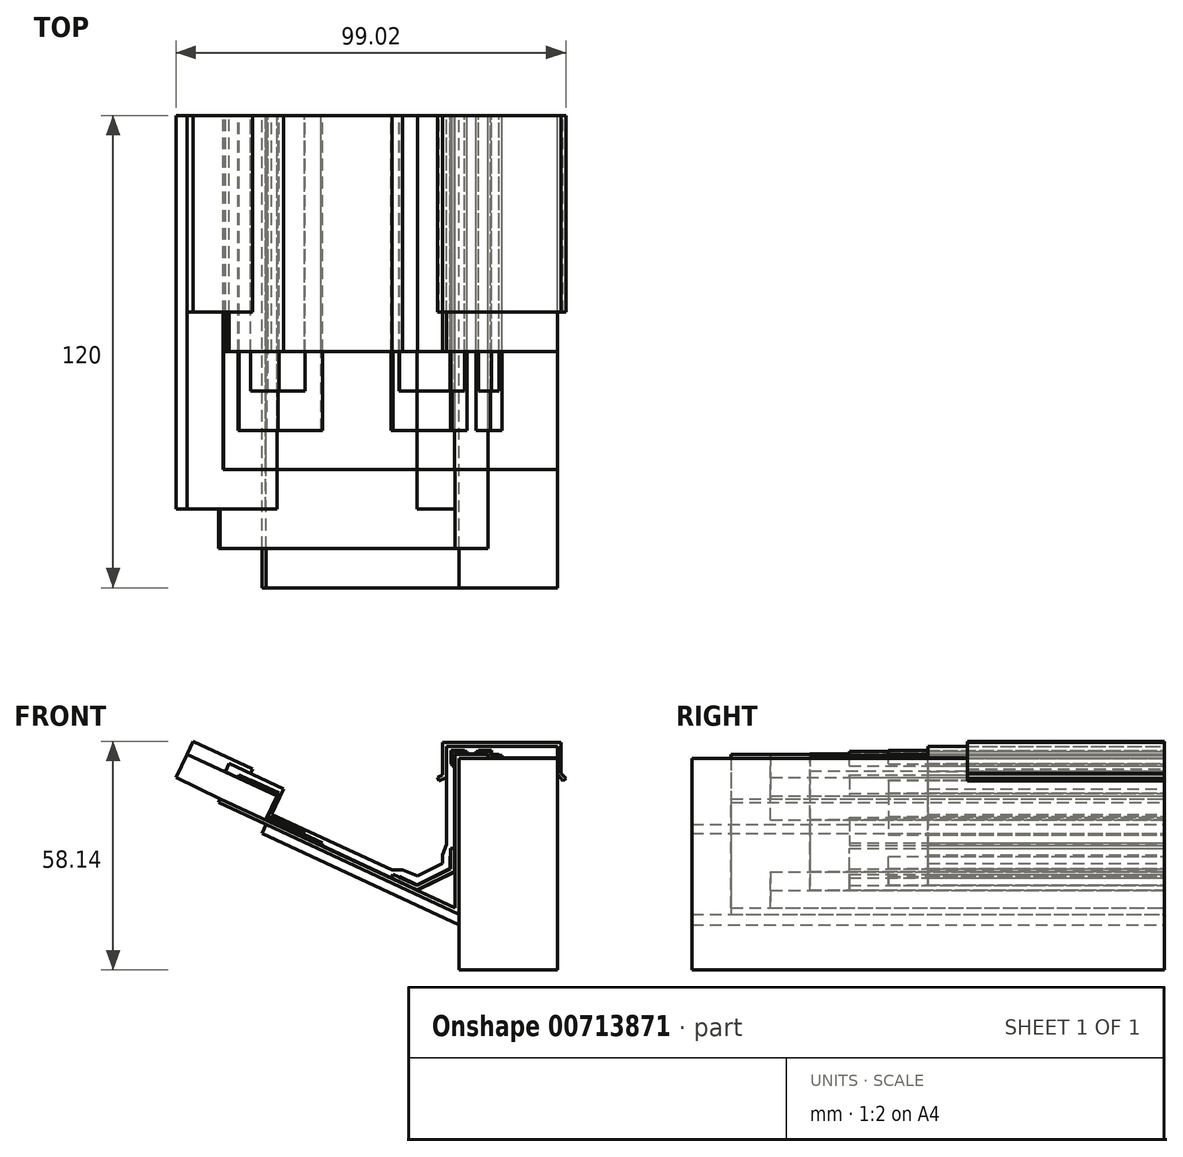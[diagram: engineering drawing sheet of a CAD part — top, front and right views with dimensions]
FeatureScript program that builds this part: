
annotation { "Feature Type Name" : "Feature", "Feature Type Description" : "" }
export const myFeature = defineFeature(function(context is Context, id is Id, definition is map)
    precondition{}
    {
        {
            var Q0;
            Q0=qCreatedBy(makeId("Front.planeOp"),FACE);
            var sketch = newSketch(context, id + "F0", { "sketchPlane" : qUnion([Q0])});
            skLineSegment(sketch, "E0.bottom", {"start": v(37.75, 38) * mm, "end": v(62.75, 38) * mm});
            skLineSegment(sketch, "E0.top", {"start": v(37.75, -15.78) * mm, "end": v(62.75, -15.78) * mm});
            skLineSegment(sketch, "E0.left", {"start": v(37.75, 38) * mm, "end": v(37.75, -15.78) * mm});
            skLineSegment(sketch, "E0.right", {"start": v(62.75, 38) * mm, "end": v(62.75, -15.78) * mm});
            skLineSegment(sketch, "E1", {"start": v(45.13, 38) * mm, "end": v(45.13, 39) * mm});
            skLineSegment(sketch, "E2", {"start": v(45.13, 39) * mm, "end": v(36.75, 39) * mm});
            skLineSegment(sketch, "E3", {"start": v(36.75, 39) * mm, "end": v(36.75, 0) * mm});
            skLineSegment(sketch, "E4", {"start": v(36.75, 0) * mm, "end": v(-22.92, 27.76) * mm});
            skLineSegment(sketch, "E5", {"start": v(-22.92, 27.76) * mm, "end": v(-23.34, 26.86) * mm});
            skLineSegment(sketch, "E6", {"start": v(-23.34, 26.86) * mm, "end": v(37.75, -1.57) * mm});
            skLineSegment(sketch, "E7", {"start": v(37.75, 38) * mm, "end": v(37.75, 40.22) * mm, "construction": true});
            skLineSegment(sketch, "E8", {"start": v(-11.3, 22.36) * mm, "end": v(-8.48, 28.43) * mm});
            skLineSegment(sketch, "E9", {"start": v(-8.48, 28.43) * mm, "end": v(-31.34, 39.07) * mm});
            skLineSegment(sketch, "E10", {"start": v(-31.34, 39.07) * mm, "end": v(-34.1, 33.15) * mm});
            skLineSegment(sketch, "E11", {"start": v(-34.1, 33.15) * mm, "end": v(-22.92, 27.76) * mm});
            skLineSegment(sketch, "E12", {"start": v(-11.24, 21.23) * mm, "end": v(-12.29, 18.98) * mm});
            skLineSegment(sketch, "E13", {"start": v(-12.29, 18.98) * mm, "end": v(37.75, -4.3) * mm});
            skLineSegment(sketch, "E14", {"start": v(27.16, 4.46) * mm, "end": v(36.75, 9.19) * mm});
            skLineSegment(sketch, "E15", {"start": v(-22.13, 34.79) * mm, "end": v(-22.09, 34.88) * mm});
            skLineSegment(sketch, "E16", {"start": v(-22.09, 34.88) * mm, "end": v(-8.43, 28.52) * mm});
            skLineSegment(sketch, "E17", {"start": v(-8.43, 28.52) * mm, "end": v(-8.48, 28.43) * mm});
            skLineSegment(sketch, "E18", {"start": v(-11.26, 22.45) * mm, "end": v(27.16, 4.57) * mm});
            skLineSegment(sketch, "E19", {"start": v(27.16, 4.57) * mm, "end": v(36.65, 9.25) * mm});
            skLineSegment(sketch, "E20", {"start": v(36.65, 9.25) * mm, "end": v(36.65, 39.1) * mm});
            skLineSegment(sketch, "E21", {"start": v(36.65, 39.1) * mm, "end": v(45.13, 39.1) * mm});
            skLineSegment(sketch, "E22", {"start": v(45.13, 39.1) * mm, "end": v(45.13, 39) * mm});
            skLineSegment(sketch, "E23", {"start": v(36.75, 39) * mm, "end": v(36.75, 39.77) * mm, "construction": true});
            skLineSegment(sketch, "E24", {"start": v(27.16, 4.57) * mm, "end": v(27.2, 4.48) * mm, "construction": true});
            skLineSegment(sketch, "E25", {"start": v(-18.36, 33.14) * mm, "end": v(-18.08, 33.75) * mm});
            skLineSegment(sketch, "E26", {"start": v(-18.08, 33.75) * mm, "end": v(-8.15, 29.13) * mm});
            skLineSegment(sketch, "E27", {"start": v(-8.15, 29.13) * mm, "end": v(-8.43, 28.52) * mm});
            skLineSegment(sketch, "E28", {"start": v(-10.98, 23.06) * mm, "end": v(3.07, 16.52) * mm});
            skLineSegment(sketch, "E29", {"start": v(3.07, 16.52) * mm, "end": v(2.79, 15.91) * mm});
            skLineSegment(sketch, "E30", {"start": v(-15.18, 32.4) * mm, "end": v(-15.1, 32.58) * mm});
            skLineSegment(sketch, "E31", {"start": v(-15.1, 32.58) * mm, "end": v(-7.89, 29.23) * mm});
            skLineSegment(sketch, "E32", {"start": v(-7.89, 29.23) * mm, "end": v(-10.67, 23.25) * mm});
            skLineSegment(sketch, "E33", {"start": v(-10.67, 23.25) * mm, "end": v(-1.32, 18.9) * mm});
            skLineSegment(sketch, "E34", {"start": v(-1.32, 18.9) * mm, "end": v(-1.45, 18.62) * mm});
            skLineSegment(sketch, "E35", {"start": v(-8.15, 29.13) * mm, "end": v(-7.97, 29.05) * mm, "construction": true});
            skLineSegment(sketch, "E36", {"start": v(20.57, 7.64) * mm, "end": v(20.99, 8.55) * mm});
            skLineSegment(sketch, "E37", {"start": v(20.99, 8.55) * mm, "end": v(27.15, 5.68) * mm});
            skLineSegment(sketch, "E38", {"start": v(27.15, 5.68) * mm, "end": v(35.65, 9.87) * mm});
            skLineSegment(sketch, "E39", {"start": v(35.65, 9.87) * mm, "end": v(35.65, 15.07) * mm});
            skLineSegment(sketch, "E40", {"start": v(35.65, 15.07) * mm, "end": v(36.65, 15.07) * mm});
            skLineSegment(sketch, "E41", {"start": v(35.65, 9.87) * mm, "end": v(36.1, 8.97) * mm, "construction": true});
            skLineSegment(sketch, "E42", {"start": v(27.15, 5.68) * mm, "end": v(27.6, 4.78) * mm, "construction": true});
            skLineSegment(sketch, "E43", {"start": v(22.39, 7.9) * mm, "end": v(22.54, 7.83) * mm});
            skLineSegment(sketch, "E44", {"start": v(22.54, 7.83) * mm, "end": v(22.62, 8) * mm});
            skLineSegment(sketch, "E45", {"start": v(22.62, 8) * mm, "end": v(27.15, 5.9) * mm});
            skLineSegment(sketch, "E46", {"start": v(27.15, 5.9) * mm, "end": v(35.45, 10) * mm});
            skLineSegment(sketch, "E47", {"start": v(35.45, 10) * mm, "end": v(35.45, 13.11) * mm});
            skLineSegment(sketch, "E48", {"start": v(35.45, 13.11) * mm, "end": v(35.65, 13.11) * mm});
            skLineSegment(sketch, "E49", {"start": v(35.45, 10) * mm, "end": v(35.54, 9.82) * mm, "construction": true});
            skLineSegment(sketch, "E50", {"start": v(27.15, 5.9) * mm, "end": v(27.15, 5.68) * mm, "construction": true});
            skLineSegment(sketch, "E51", {"start": v(36.65, 36.13) * mm, "end": v(35.98, 36.13) * mm});
            skLineSegment(sketch, "E52", {"start": v(35.98, 36.13) * mm, "end": v(35.98, 39.78) * mm});
            skLineSegment(sketch, "E53", {"start": v(35.98, 39.78) * mm, "end": v(39.8, 39.77) * mm});
            skLineSegment(sketch, "E54", {"start": v(39.8, 39.77) * mm, "end": v(39.8, 39.1) * mm});
            skLineSegment(sketch, "E55", {"start": v(42.12, 39.1) * mm, "end": v(42.12, 39.77) * mm});
            skLineSegment(sketch, "E56", {"start": v(42.12, 39.77) * mm, "end": v(45.8, 39.77) * mm});
            skLineSegment(sketch, "E57", {"start": v(45.13, 39.1) * mm, "end": v(45.13, 39.77) * mm, "construction": true});
            skLineSegment(sketch, "E58", {"start": v(35.98, 36.62) * mm, "end": v(35.78, 36.62) * mm});
            skLineSegment(sketch, "E59", {"start": v(35.78, 36.62) * mm, "end": v(35.78, 39.97) * mm});
            skLineSegment(sketch, "E60", {"start": v(35.78, 39.97) * mm, "end": v(39.22, 39.97) * mm});
            skLineSegment(sketch, "E61", {"start": v(39.22, 39.97) * mm, "end": v(39.22, 39.77) * mm});
            skLineSegment(sketch, "E62", {"start": v(42.72, 39.77) * mm, "end": v(42.72, 39.97) * mm});
            skLineSegment(sketch, "E63", {"start": v(45.13, 38.1) * mm, "end": v(62.75, 38.1) * mm});
            skLineSegment(sketch, "E64", {"start": v(62.75, 38.1) * mm, "end": v(62.75, 38) * mm});
            skLineSegment(sketch, "E65", {"start": v(45.8, 39.77) * mm, "end": v(45.8, 38.77) * mm});
            skLineSegment(sketch, "E66", {"start": v(45.8, 38.77) * mm, "end": v(48.67, 38.77) * mm});
            skLineSegment(sketch, "E67", {"start": v(48.67, 38.77) * mm, "end": v(48.67, 38.1) * mm});
            skLineSegment(sketch, "E68", {"start": v(42.72, 39.97) * mm, "end": v(46, 39.97) * mm});
            skLineSegment(sketch, "E69", {"start": v(46, 39.97) * mm, "end": v(46, 38.97) * mm});
            skLineSegment(sketch, "E70", {"start": v(46, 38.97) * mm, "end": v(47.95, 38.97) * mm});
            skLineSegment(sketch, "E71", {"start": v(47.95, 38.97) * mm, "end": v(47.95, 38.77) * mm});
            skLineSegment(sketch, "E72", {"start": v(45.8, 39.61) * mm, "end": v(46, 39.61) * mm, "construction": true});
            skLineSegment(sketch, "E73", {"start": v(-21.56, 34.63) * mm, "end": v(-20.6, 36.68) * mm});
            skLineSegment(sketch, "E74", {"start": v(-20.6, 36.68) * mm, "end": v(-6.84, 30.28) * mm});
            skLineSegment(sketch, "E75", {"start": v(-6.84, 30.28) * mm, "end": v(-9.89, 23.74) * mm});
            skLineSegment(sketch, "E76", {"start": v(-9.89, 23.74) * mm, "end": v(20.81, 9.62) * mm});
            skLineSegment(sketch, "E77", {"start": v(34.65, 16.2) * mm, "end": v(34.65, 41.1) * mm});
            skLineSegment(sketch, "E78", {"start": v(34.65, 41.1) * mm, "end": v(46.3, 41.1) * mm});
            skLineSegment(sketch, "E79", {"start": v(46.3, 41.1) * mm, "end": v(47.1, 41.1) * mm});
            skLineSegment(sketch, "E80", {"start": v(47.1, 41.1) * mm, "end": v(62.75, 41.1) * mm});
            skLineSegment(sketch, "E81", {"start": v(62.75, 41.1) * mm, "end": v(62.75, 38.1) * mm});
            skLineSegment(sketch, "E82", {"start": v(41.21, 39.1) * mm, "end": v(41.21, 41.1) * mm, "construction": true});
            skLineSegment(sketch, "E83", {"start": v(36.65, 32.37) * mm, "end": v(34.65, 32.37) * mm, "construction": true});
            skLineSegment(sketch, "E84", {"start": v(20.81, 9.62) * mm, "end": v(23.42, 9.62) * mm});
            skLineSegment(sketch, "E85", {"start": v(23.42, 9.62) * mm, "end": v(27.28, 8.2) * mm});
            skLineSegment(sketch, "E86", {"start": v(27.28, 8.2) * mm, "end": v(33.65, 11.34) * mm});
            skLineSegment(sketch, "E87", {"start": v(33.65, 11.34) * mm, "end": v(33.65, 13.5) * mm});
            skLineSegment(sketch, "E88", {"start": v(33.65, 13.5) * mm, "end": v(34.65, 16.2) * mm});
            skLineSegment(sketch, "E89", {"start": v(20.81, 9.62) * mm, "end": v(19.97, 7.8) * mm, "construction": true});
            skLineSegment(sketch, "E90", {"start": v(19.97, 7.8) * mm, "end": v(19.73, 8.1) * mm, "construction": true});
            skLineSegment(sketch, "E91", {"start": v(34.65, 16.2) * mm, "end": v(36.65, 16.2) * mm, "construction": true});
            skLineSegment(sketch, "E92", {"start": v(33.65, 13.5) * mm, "end": v(35.65, 13.5) * mm, "construction": true});
            skLineSegment(sketch, "E93", {"start": v(33.65, 11.34) * mm, "end": v(34.54, 9.54) * mm, "construction": true});
            skLineSegment(sketch, "E94", {"start": v(34.54, 9.54) * mm, "end": v(34.41, 9.65) * mm, "construction": true});
            skLineSegment(sketch, "E95", {"start": v(23.42, 9.62) * mm, "end": v(22.58, 7.8) * mm, "construction": true});
            skLineSegment(sketch, "E96", {"start": v(22.58, 7.8) * mm, "end": v(22.51, 7.96) * mm, "construction": true});
            skLineSegment(sketch, "E97", {"start": v(27.28, 8.2) * mm, "end": v(28.23, 6.44) * mm, "construction": true});
            skLineSegment(sketch, "E98", {"start": v(34.65, 33.12) * mm, "end": v(32.74, 32.27) * mm});
            skLineSegment(sketch, "E99", {"start": v(32.74, 32.27) * mm, "end": v(32.33, 33.18) * mm});
            skLineSegment(sketch, "E100", {"start": v(32.33, 33.18) * mm, "end": v(33.65, 33.77) * mm});
            skLineSegment(sketch, "E101", {"start": v(33.65, 33.77) * mm, "end": v(33.65, 42.1) * mm});
            skLineSegment(sketch, "E102", {"start": v(33.65, 42.1) * mm, "end": v(63.75, 42.1) * mm});
            skLineSegment(sketch, "E103", {"start": v(63.75, 42.1) * mm, "end": v(63.75, 34.16) * mm});
            skLineSegment(sketch, "E104", {"start": v(63.75, 34.16) * mm, "end": v(64.93, 32.86) * mm});
            skLineSegment(sketch, "E105", {"start": v(64.93, 32.86) * mm, "end": v(64.27, 32.26) * mm});
            skLineSegment(sketch, "E106", {"start": v(64.27, 32.26) * mm, "end": v(62.75, 33.94) * mm});
            skLineSegment(sketch, "E107", {"start": v(33.65, 33.77) * mm, "end": v(34.65, 33.77) * mm, "construction": true});
            skLineSegment(sketch, "E108", {"start": v(34.65, 41.1) * mm, "end": v(33.65, 41.1) * mm, "construction": true});
            skLineSegment(sketch, "E109", {"start": v(62.75, 41.1) * mm, "end": v(63.75, 41.1) * mm, "construction": true});
            skLineSegment(sketch, "E110", {"start": v(63.75, 34.16) * mm, "end": v(62.75, 34.16) * mm, "construction": true});
            skLineSegment(sketch, "E111", {"start": v(-15.22, 34.18) * mm, "end": v(-14.68, 35.32) * mm});
            skLineSegment(sketch, "E112", {"start": v(-14.68, 35.32) * mm, "end": v(-29.8, 42.36) * mm});
            skLineSegment(sketch, "E113", {"start": v(-29.8, 42.36) * mm, "end": v(-31.34, 39.07) * mm});
            skSolve(sketch);
        }
        {
            var Q0;
            {var subQ4=sQuery(id+"F0.wireOp",EDGE,"E0.top");Q0=makeQuery(id+"F0.imprint","IMPRINT",FACE,{"disambiguationData":[TD([[makeQuery(id+"F0.imprint","IMPRINT",EDGE,{"derivedFrom":subQ4}),1.0]])]});}
            extrude(context, id + "F1", {"entities" : qUnion([Q0]), "depth" : 120 * mm});
        }
        {
            var Q0;
            {var subQ4=sQuery(id+"F0.wireOp",EDGE,"E12");Q0=makeQuery(id+"F0.imprint","IMPRINT",FACE,{"disambiguationData":[TD([[makeQuery(id+"F0.imprint","IMPRINT",EDGE,{"derivedFrom":subQ4}),1.0]])]});}
            extrude(context, id + "F2", {"entities" : qUnion([Q0]), "depth" : 120 * mm});
        }
        {
            var Q0;
            {var subQ8=sQuery(id+"F0.wireOp",EDGE,"E2");Q0=makeQuery(id+"F0.imprint","IMPRINT",FACE,{"disambiguationData":[TD([[makeQuery(id+"F0.imprint","IMPRINT",EDGE,{"derivedFrom":subQ8}),1.0]])]});}
            extrude(context, id + "F3", {"entities" : qUnion([Q0]), "depth" : 110 * mm});
        }
        {
            var Q0;
            {var subQ9=sQuery(id+"F0.wireOp",EDGE,"E10");Q0=makeQuery(id+"F0.imprint","IMPRINT",FACE,{"disambiguationData":[TD([[makeQuery(id+"F0.imprint","IMPRINT",EDGE,{"derivedFrom":subQ9}),1.0]])]});}
            extrude(context, id + "F4", {"entities" : qUnion([Q0]), "depth" : 100 * mm});
        }
        {
            var Q0;
            {var subQ3=sQuery(id+"F0.wireOp",EDGE,"E14");Q0=makeQuery(id+"F0.imprint","IMPRINT",FACE,{"disambiguationData":[TD([[makeQuery(id+"F0.imprint","IMPRINT",EDGE,{"derivedFrom":subQ3}),-1.0]])]});}
            extrude(context, id + "F5", {"entities" : qUnion([Q0]), "depth" : 100 * mm});
        }
        {
            var Q0;
            {var subQ3=sQuery(id+"F0.wireOp",EDGE,"E15");Q0=makeQuery(id+"F0.imprint","IMPRINT",FACE,{"disambiguationData":[TD([[makeQuery(id+"F0.imprint","IMPRINT",EDGE,{"derivedFrom":subQ3}),-1.0]])]});}
            extrude(context, id + "F6", {"entities" : qUnion([Q0]), "depth" : 90 * mm});
        }
        {
            var Q0;
            {var subQ12=sQuery(id+"F0.wireOp",EDGE,"E2");Q0=makeQuery(id+"F0.imprint","IMPRINT",FACE,{"disambiguationData":[TD([[makeQuery(id+"F0.imprint","IMPRINT",EDGE,{"derivedFrom":subQ12}),-1.0]])]});}
            extrude(context, id + "F7", {"entities" : qUnion([Q0]), "depth" : 90 * mm});
        }
        {
            var Q0;
            {var subQ0=sQuery(id+"F0.wireOp",EDGE,"E64");Q0=makeQuery(id+"F0.imprint","IMPRINT",FACE,{"disambiguationData":[TD([[makeQuery(id+"F0.imprint","IMPRINT",EDGE,{"derivedFrom":subQ0}),-1.0]])]});}
            extrude(context, id + "F8", {"entities" : qUnion([Q0]), "depth" : 90 * mm});
        }
        {
            var Q0;
            {var subQ1=sQuery(id+"F0.wireOp",EDGE,"E25");Q0=makeQuery(id+"F0.imprint","IMPRINT",FACE,{"disambiguationData":[TD([[makeQuery(id+"F0.imprint","IMPRINT",EDGE,{"derivedFrom":subQ1}),-1.0]])]});}
            extrude(context, id + "F9", {"entities" : qUnion([Q0]), "depth" : 80 * mm});
        }
        {
            var Q0;
            {var subQ6=sQuery(id+"F0.wireOp",EDGE,"E29");Q0=makeQuery(id+"F0.imprint","IMPRINT",FACE,{"disambiguationData":[TD([[makeQuery(id+"F0.imprint","IMPRINT",EDGE,{"derivedFrom":subQ6}),-1.0]])]});}
            extrude(context, id + "F10", {"entities" : qUnion([Q0]), "depth" : 80 * mm});
        }
        {
            var Q0;
            {var subQ5=sQuery(id+"F0.wireOp",EDGE,"E19");Q0=makeQuery(id+"F0.imprint","IMPRINT",FACE,{"disambiguationData":[TD([[makeQuery(id+"F0.imprint","IMPRINT",EDGE,{"derivedFrom":subQ5}),1.0]])]});}
            extrude(context, id + "F11", {"entities" : qUnion([Q0]), "depth" : 80 * mm});
        }
        {
            var Q0;
            {var subQ1=sQuery(id+"F0.wireOp",EDGE,"E51");Q0=makeQuery(id+"F0.imprint","IMPRINT",FACE,{"disambiguationData":[TD([[makeQuery(id+"F0.imprint","IMPRINT",EDGE,{"derivedFrom":subQ1}),-1.0]])]});}
            extrude(context, id + "F12", {"entities" : qUnion([Q0]), "depth" : 80 * mm});
        }
        {
            var Q0;
            {var subQ6=sQuery(id+"F0.wireOp",EDGE,"E22");Q0=makeQuery(id+"F0.imprint","IMPRINT",FACE,{"disambiguationData":[TD([[makeQuery(id+"F0.imprint","IMPRINT",EDGE,{"derivedFrom":subQ6}),1.0]])]});}
            extrude(context, id + "F13", {"entities" : qUnion([Q0]), "depth" : 80 * mm});
        }
        {
            var Q0;
            {var subQ3=sQuery(id+"F0.wireOp",EDGE,"E17");Q0=makeQuery(id+"F0.imprint","IMPRINT",FACE,{"disambiguationData":[TD([[makeQuery(id+"F0.imprint","IMPRINT",EDGE,{"derivedFrom":subQ3}),1.0]])]});}
            extrude(context, id + "F14", {"entities" : qUnion([Q0]), "depth" : 70 * mm});
        }
        {
            var Q0;
            {var subQ1=sQuery(id+"F0.wireOp",EDGE,"E38");Q0=makeQuery(id+"F0.imprint","IMPRINT",FACE,{"disambiguationData":[TD([[makeQuery(id+"F0.imprint","IMPRINT",EDGE,{"derivedFrom":subQ1}),1.0]])]});}
            extrude(context, id + "F15", {"entities" : qUnion([Q0]), "depth" : 70 * mm});
        }
        {
            var Q0;
            {var subQ0=sQuery(id+"F0.wireOp",EDGE,"E58");Q0=makeQuery(id+"F0.imprint","IMPRINT",FACE,{"disambiguationData":[TD([[makeQuery(id+"F0.imprint","IMPRINT",EDGE,{"derivedFrom":subQ0}),-1.0]])]});}
            extrude(context, id + "F16", {"entities" : qUnion([Q0]), "depth" : 70 * mm});
        }
        {
            var Q0;
            {var subQ3=sQuery(id+"F0.wireOp",EDGE,"E62");Q0=makeQuery(id+"F0.imprint","IMPRINT",FACE,{"disambiguationData":[TD([[makeQuery(id+"F0.imprint","IMPRINT",EDGE,{"derivedFrom":subQ3}),-1.0]])]});}
            extrude(context, id + "F17", {"entities" : qUnion([Q0]), "depth" : 70 * mm});
        }
        {
            var Q0;
            {var subQ20=sQuery(id+"F0.wireOp",EDGE,"E25");Q0=makeQuery(id+"F0.imprint","IMPRINT",FACE,{"disambiguationData":[TD([[makeQuery(id+"F0.imprint","IMPRINT",EDGE,{"derivedFrom":subQ20}),1.0]])]});}
            extrude(context, id + "F18", {"entities" : qUnion([Q0]), "depth" : 60 * mm});
        }
        {
            var Q0;
            {var subQ1=sQuery(id+"F0.wireOp",EDGE,"E64");Q0=makeQuery(id+"F0.imprint","IMPRINT",FACE,{"disambiguationData":[TD([[makeQuery(id+"F0.imprint","IMPRINT",EDGE,{"derivedFrom":subQ1}),1.0]])]});}
            extrude(context, id + "F19", {"entities" : qUnion([Q0]), "depth" : 50 * mm});
        }
        {
            var Q0;
            {var subQ1=sQuery(id+"F0.wireOp",EDGE,"E15");Q0=makeQuery(id+"F0.imprint","IMPRINT",FACE,{"disambiguationData":[TD([[makeQuery(id+"F0.imprint","IMPRINT",EDGE,{"derivedFrom":subQ1}),1.0]])]});}
            extrude(context, id + "F20", {"entities" : qUnion([Q0]), "depth" : 50 * mm});
        }
    });
